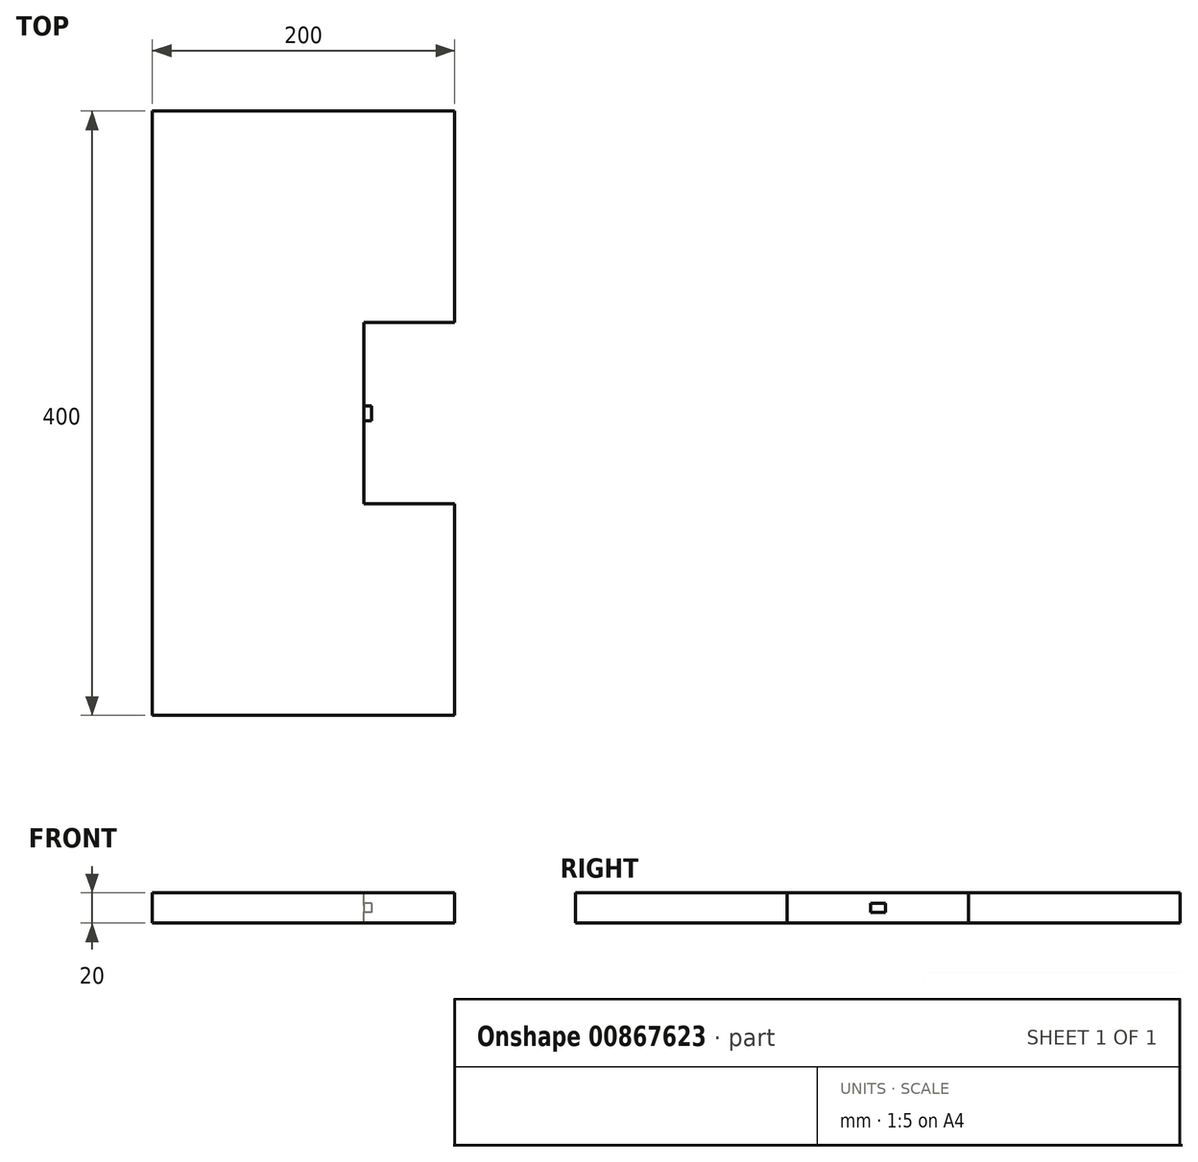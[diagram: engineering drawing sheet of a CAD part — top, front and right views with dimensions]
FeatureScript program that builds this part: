
annotation { "Feature Type Name" : "Feature", "Feature Type Description" : "" }
export const myFeature = defineFeature(function(context is Context, id is Id, definition is map)
    precondition{}
    {
        {
            var Q0;
            Q0=qCreatedBy(makeId("Front.planeOp"),FACE);
            var sketch = newSketch(context, id + "F0", { "sketchPlane" : qUnion([Q0])});
            skLineSegment(sketch, "E0", {"start": v(0, 0) * mm, "end": v(0, 20) * mm});
            skLineSegment(sketch, "E1", {"start": v(0, 20) * mm, "end": v(200, 20) * mm});
            skLineSegment(sketch, "E2", {"start": v(200, 20) * mm, "end": v(200, 0) * mm});
            skLineSegment(sketch, "E3", {"start": v(200, 0) * mm, "end": v(0, 0) * mm});
            skSolve(sketch);
        }
        {
            var Q0;
            Q0=makeQuery(id+"F0.imprint","IMPRINT",FACE,{"disambiguationData":[TD([[makeQuery(id+"F0.imprint","IMPRINT",EDGE,{"derivedFrom":sQuery(id+"F0.wireOp",EDGE,"E0")}),-1.0]])]});
            extrude(context, id + "F1", {"entities" : qUnion([Q0]), "depth" : 400 * mm, "offsetDistance" : 25.4 * mm});
        }
        {
            var Q0;
            Q0=makeQuery(id+"F1.opExtrude","SWEPT_FACE",FACE,{"disambiguationData":[OSD([sQuery(id+"F0.wireOp",EDGE,"E1")])]});
            var sketch = newSketch(context, id + "F2", { "sketchPlane" : qUnion([Q0])});
            skLineSegment(sketch, "E4", {"start": v(200, -200) * mm, "end": v(200, -260) * mm});
            skLineSegment(sketch, "E5", {"start": v(200, -260) * mm, "end": v(140, -260) * mm});
            skLineSegment(sketch, "E6", {"start": v(140, -260) * mm, "end": v(140, -140) * mm});
            skLineSegment(sketch, "E7", {"start": v(140, -140) * mm, "end": v(200, -140) * mm});
            skLineSegment(sketch, "E8", {"start": v(200, -140) * mm, "end": v(200, -200) * mm});
            skSolve(sketch);
        }
        {
            var Q0;
            Q0=makeQuery(id+"F2.imprint","IMPRINT",FACE,{"disambiguationData":[TD([[makeQuery(id+"F2.imprint","IMPRINT",EDGE,{"derivedFrom":sQuery(id+"F2.wireOp",EDGE,"E4")}),1.0]])]});
            extrude(context, id + "F3", {"entities" : qUnion([Q0]), "operationType" : NewBodyOperationType.REMOVE, "oppositeDirection" : true, "depth" : 25 * mm, "offsetDistance" : 25 * mm});
        }
        {
            var Q0;
            Q0=makeQuery(id+"F3.boolean.opBoolean","COPY",FACE,{"derivedFrom":makeQuery(id+"F3.opExtrude","SWEPT_FACE",FACE,{"disambiguationData":[OSD([sQuery(id+"F2.wireOp",EDGE,"E6")])]})});
            var sketch = newSketch(context, id + "F4", { "sketchPlane" : qUnion([Q0])});
            skLineSegment(sketch, "E9", {"start": v(-205, 13) * mm, "end": v(-205, 7) * mm});
            skLineSegment(sketch, "E10", {"start": v(-205, 7) * mm, "end": v(-195, 7) * mm});
            skLineSegment(sketch, "E11", {"start": v(-195, 7) * mm, "end": v(-195, 13) * mm});
            skLineSegment(sketch, "E12", {"start": v(-195, 13) * mm, "end": v(-205, 13) * mm});
            skSolve(sketch);
        }
        {
            var Q0;
            Q0=makeQuery(id+"F4.imprint","IMPRINT",FACE,{"disambiguationData":[TD([[makeQuery(id+"F4.imprint","IMPRINT",EDGE,{"derivedFrom":sQuery(id+"F4.wireOp",EDGE,"E9")}),1.0]])]});
            extrude(context, id + "F5", {"entities" : qUnion([Q0]), "operationType" : NewBodyOperationType.ADD, "depth" : 5 * mm, "offsetDistance" : 25 * mm});
        }
    });
